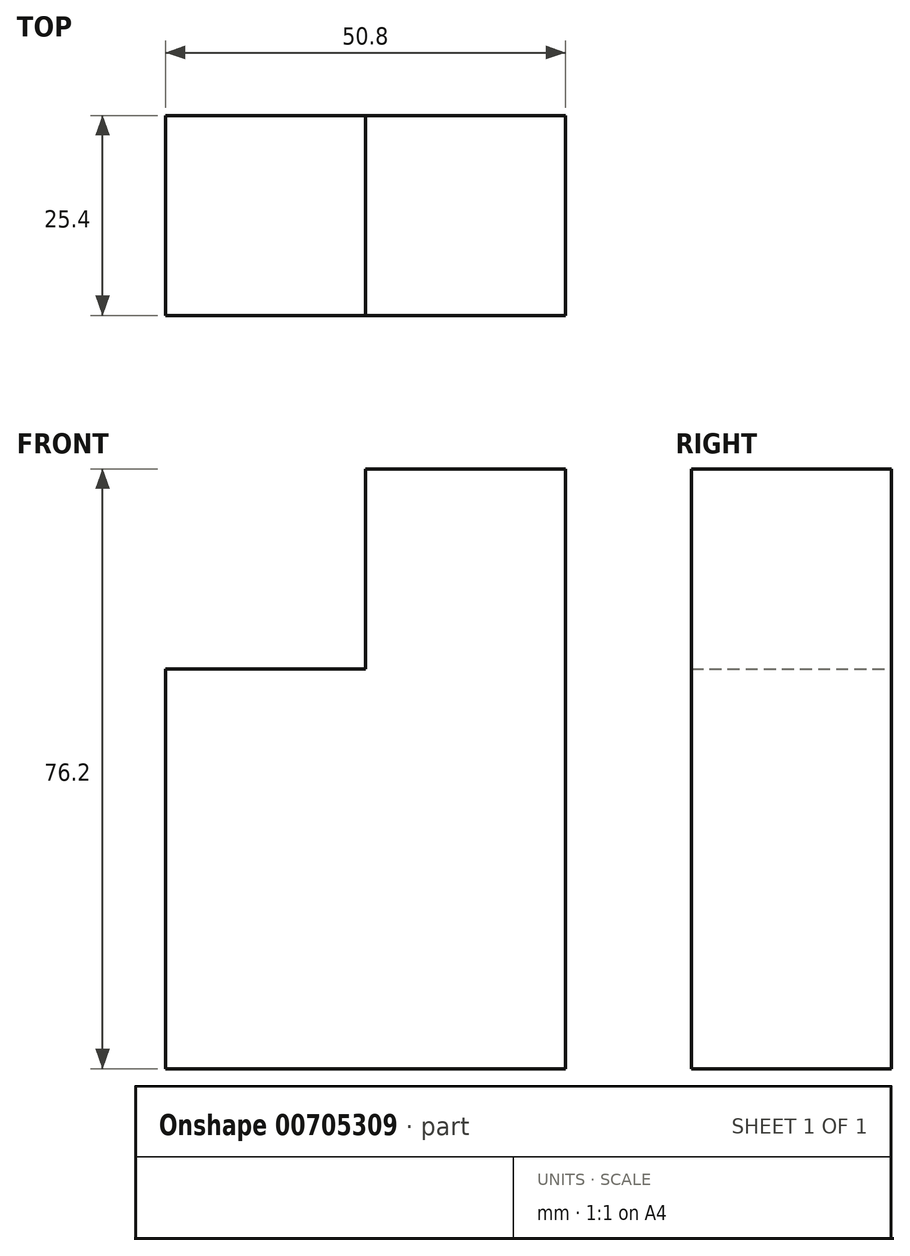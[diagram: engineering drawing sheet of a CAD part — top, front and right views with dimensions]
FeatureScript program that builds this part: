
annotation { "Feature Type Name" : "Feature", "Feature Type Description" : "" }
export const myFeature = defineFeature(function(context is Context, id is Id, definition is map)
    precondition{}
    {
        {
            var Q0;
            Q0=qCreatedBy(makeId("Front.planeOp"),FACE);
            var sketch = newSketch(context, id + "F0", { "sketchPlane" : qUnion([Q0])});
            skLineSegment(sketch, "E0.bottom", {"start": v(0, 0) * mm, "end": v(25.4, 0) * mm});
            skLineSegment(sketch, "E0.top", {"start": v(0, -25.4) * mm, "end": v(25.4, -25.4) * mm});
            skLineSegment(sketch, "E0.left", {"start": v(0, 0) * mm, "end": v(0, -25.4) * mm});
            skLineSegment(sketch, "E0.right", {"start": v(25.4, 0) * mm, "end": v(25.4, -25.4) * mm});
            skLineSegment(sketch, "E1.bottom", {"start": v(0, 0) * mm, "end": v(-25.4, 0) * mm});
            skLineSegment(sketch, "E1.top", {"start": v(0, -25.4) * mm, "end": v(-25.4, -25.4) * mm});
            skLineSegment(sketch, "E1.right", {"start": v(-25.4, 0) * mm, "end": v(-25.4, -25.4) * mm});
            skLineSegment(sketch, "E2.bottom", {"start": v(-25.4, 0) * mm, "end": v(0, 0) * mm});
            skLineSegment(sketch, "E2.top", {"start": v(-25.4, 25.4) * mm, "end": v(0, 25.4) * mm});
            skLineSegment(sketch, "E2.left", {"start": v(-25.4, 0) * mm, "end": v(-25.4, 25.4) * mm});
            skLineSegment(sketch, "E2.right", {"start": v(0, 0) * mm, "end": v(0, 25.4) * mm});
            skLineSegment(sketch, "E3.bottom", {"start": v(0, 25.4) * mm, "end": v(25.4, 25.4) * mm});
            skLineSegment(sketch, "E3.left", {"start": v(0, 25.4) * mm, "end": v(0, 0) * mm});
            skLineSegment(sketch, "E3.right", {"start": v(25.4, 25.4) * mm, "end": v(25.4, 0) * mm});
            skLineSegment(sketch, "E4.bottom", {"start": v(25.4, 25.4) * mm, "end": v(0, 25.4) * mm});
            skLineSegment(sketch, "E4.top", {"start": v(25.4, 50.8) * mm, "end": v(0, 50.8) * mm});
            skLineSegment(sketch, "E4.left", {"start": v(25.4, 25.4) * mm, "end": v(25.4, 50.8) * mm});
            skLineSegment(sketch, "E4.right", {"start": v(0, 25.4) * mm, "end": v(0, 50.8) * mm});
            skSolve(sketch);
        }
        {
            var Q0;
            Q0 = qSketchRegion(id + "F0", true);
            extrude(context, id + "F1", {"entities" : qUnion([Q0]), "depth" : 25.4 * mm, "offsetDistance" : 25.4 * mm});
        }
    });
